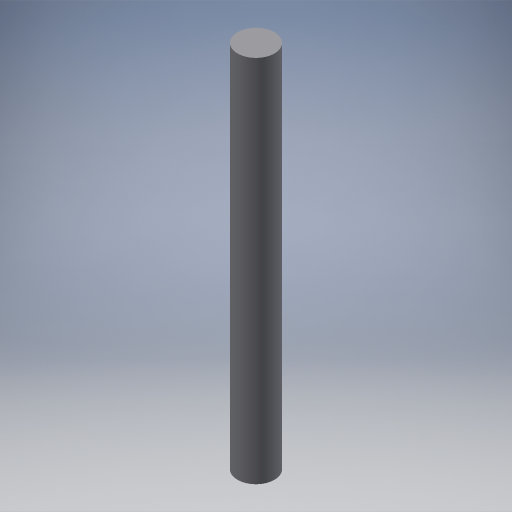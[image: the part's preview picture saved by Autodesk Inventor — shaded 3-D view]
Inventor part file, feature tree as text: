
AUTODESK INVENTOR PART (.ipt)
format: ipt  version: 2024.3 (Build 283343000, 343)  size: 242,176 bytes
history: native  units: mm
features: extrude x1
ambient origin geometry x8: Origin, YZ Plane, XZ Plane, XY Plane, X Axis, Y Axis, Z Axis, Center Point
bodies: Volumenkörper1 (feature_tree)
feature tree (1):
  extrude  "Extrusion1"  Depth=10.0mm
